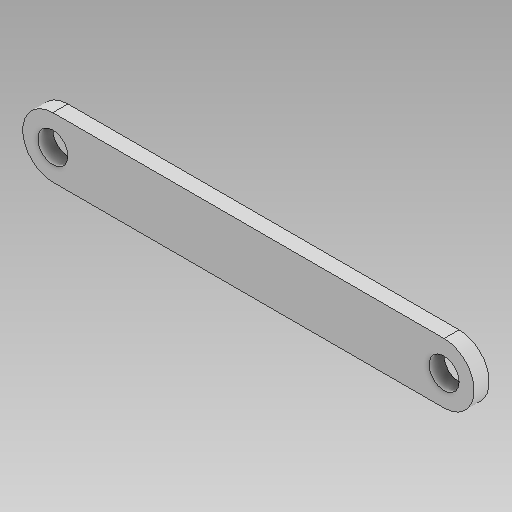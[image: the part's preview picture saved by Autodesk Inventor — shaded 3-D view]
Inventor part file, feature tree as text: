
AUTODESK INVENTOR PART (.ipt)
format: ipt  version: 2025 (Build 290162000, 162)  size: 93,184 bytes
history: native  units: in
note: dims shown in document units (in); Inventor stores cm internally (conversion verified against a paired STEP export)
features: other x1, extrude x1, sketch x1
ambient origin geometry x8: Origin, YZ Plane, XZ Plane, XY Plane, X Axis, Y Axis, Z Axis, Center Point
bodies: Body1 (feature_tree)
feature tree (3):
  other  "솔리드1"
  extrude  "돌출1"  Depth=0.7874in
  sketch  "스케치1"
